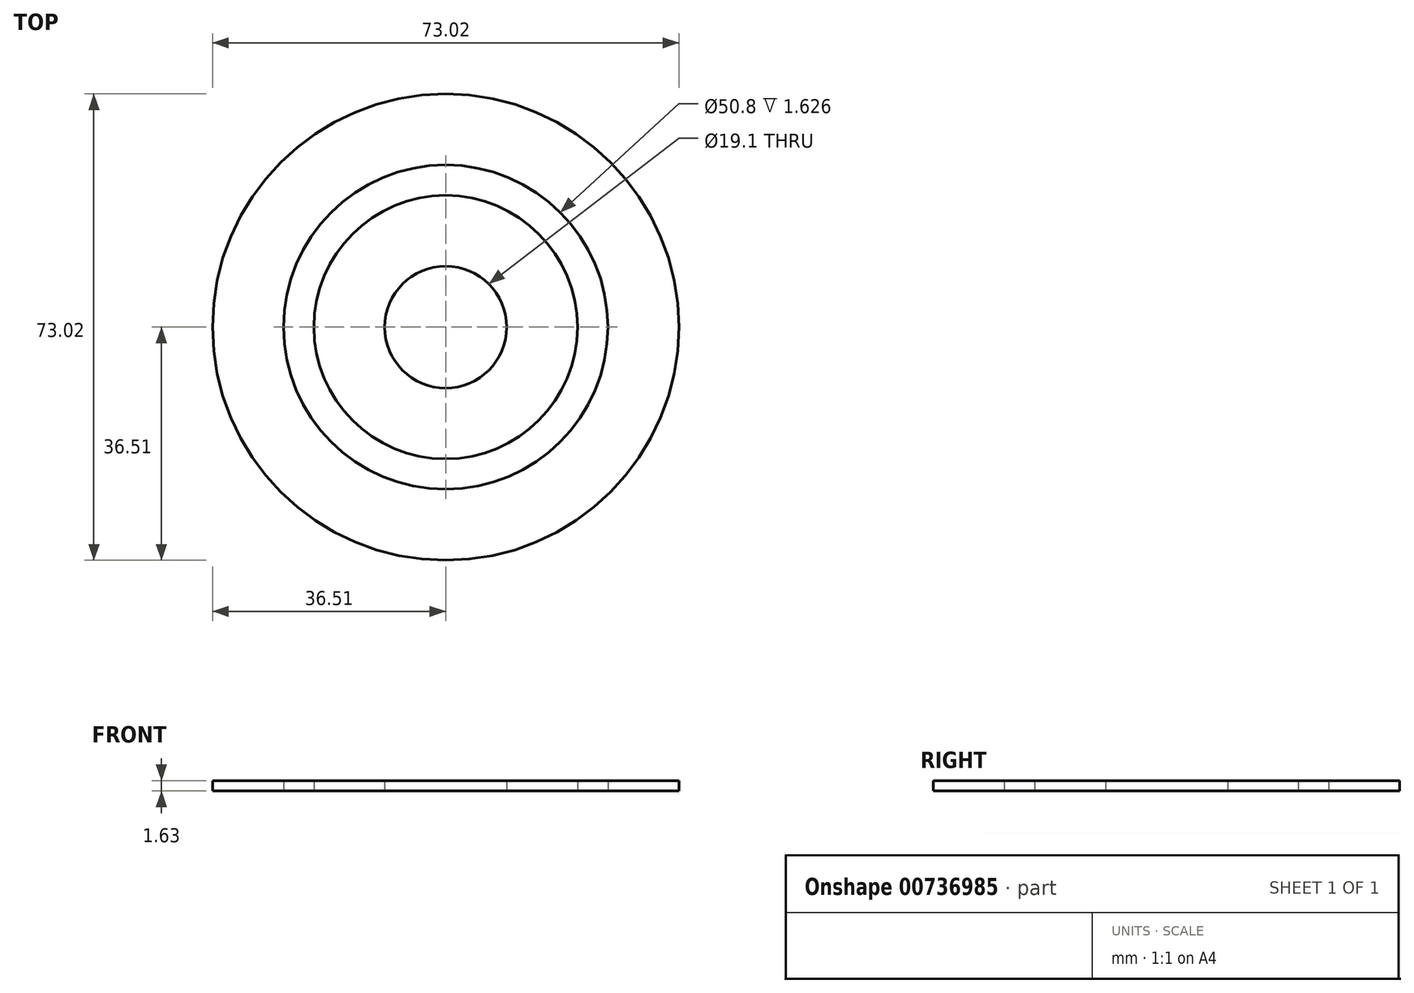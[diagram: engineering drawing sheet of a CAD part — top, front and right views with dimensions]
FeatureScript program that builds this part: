
annotation { "Feature Type Name" : "Feature", "Feature Type Description" : "" }
export const myFeature = defineFeature(function(context is Context, id is Id, definition is map)
    precondition{}
    {
        {
            var Q0;
            Q0=qCreatedBy(makeId("Top.planeOp"),FACE);
            var sketch = newSketch(context, id + "F0", { "sketchPlane" : qUnion([Q0])});
            skCircle(sketch, "E0", {"center": v(0, 0) * mm, "radius": 25.4 * mm});
            skCircle(sketch, "E1", {"center": v(0, 0) * mm, "radius": 36.51 * mm});
            skCircle(sketch, "E2", {"center": v(0, 0) * mm, "radius": 9.55 * mm});
            skCircle(sketch, "E3", {"center": v(0, 0) * mm, "radius": 20.64 * mm});
            skSolve(sketch);
        }
        {
            var Q0;
            Q0=makeQuery(id+"F0.imprint","IMPRINT",FACE,{"disambiguationData":[TD([[makeQuery(id+"F0.imprint","IMPRINT",EDGE,{"derivedFrom":sQuery(id+"F0.wireOp",EDGE,"E0")}),-1.0]])]});
            var Q1;
            Q1=makeQuery(id+"F0.imprint","IMPRINT",FACE,{"disambiguationData":[TD([[makeQuery(id+"F0.imprint","IMPRINT",EDGE,{"derivedFrom":sQuery(id+"F0.wireOp",EDGE,"E2")}),-1.0]])]});
            extrude(context, id + "F1", {"entities" : qUnion([Q0, Q1]), "depth" : 1.63 * mm, "offsetDistance" : 25.4 * mm});
        }
    });
